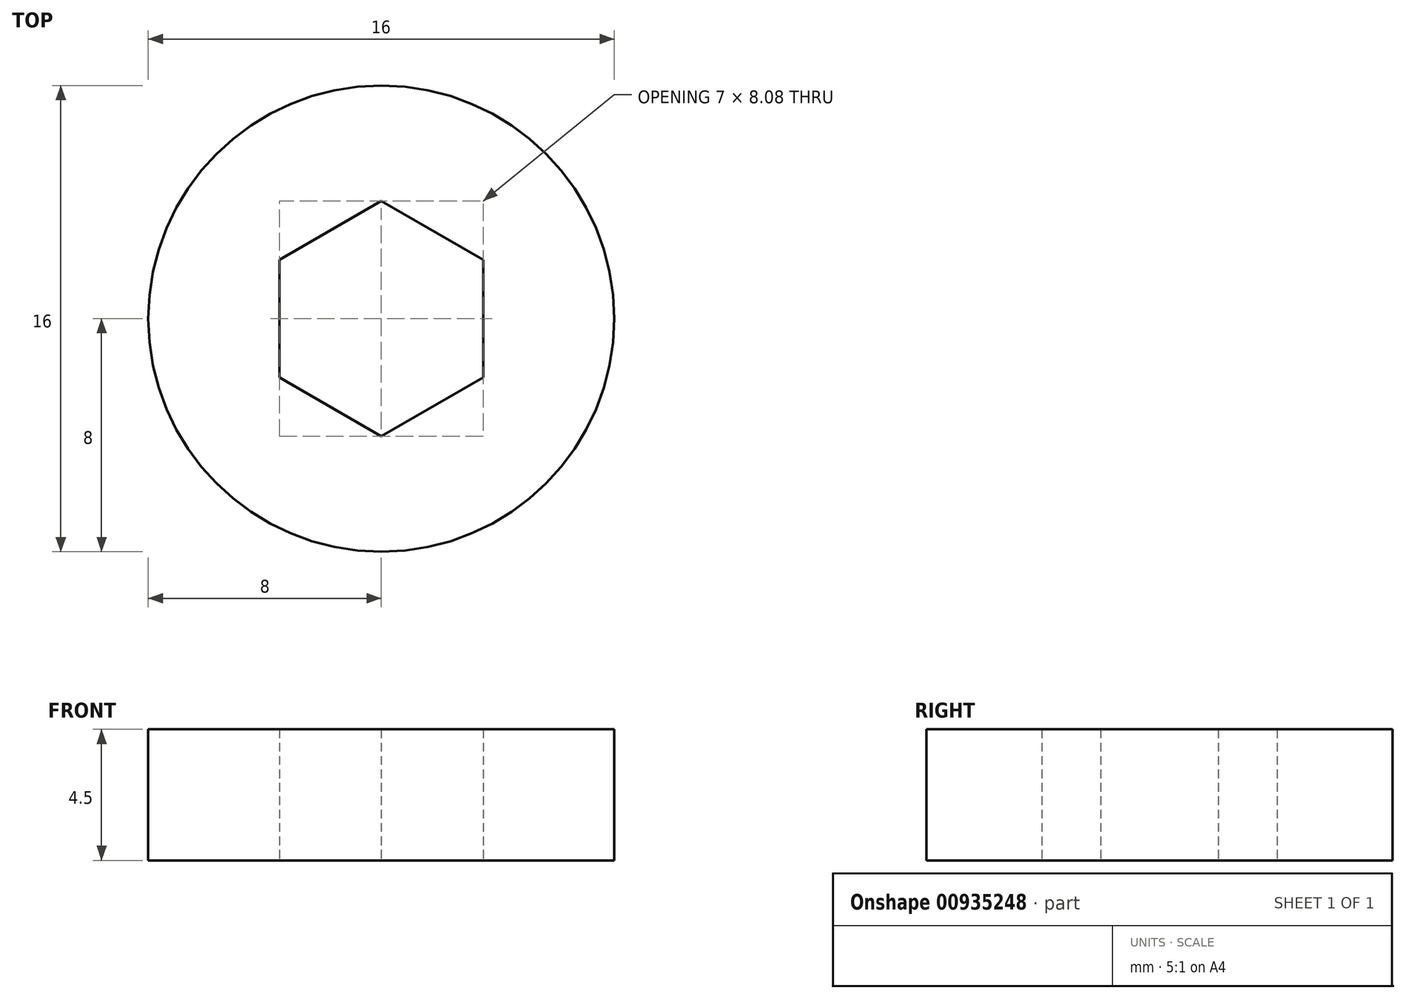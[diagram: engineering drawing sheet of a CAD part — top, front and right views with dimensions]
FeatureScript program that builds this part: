
annotation { "Feature Type Name" : "Feature", "Feature Type Description" : "" }
export const myFeature = defineFeature(function(context is Context, id is Id, definition is map)
    precondition{}
    {
        {
            var Q0;
            Q0=qCreatedBy(makeId("Top.planeOp"),FACE);
            var sketch = newSketch(context, id + "F0", { "sketchPlane" : qUnion([Q0])});
            skCircle(sketch, "E0", {"center": v(0, 0) * mm, "radius": 8 * mm});
            skCircle(sketch, "E1", {"center": v(0, 0) * mm, "radius": 3.5 * mm});
            skCircle(sketch, "E2.cCircle", {"center": v(0, 0) * mm, "radius": 3.5 * mm, "construction": true});
            skLineSegment(sketch, "E2.0", {"start": v(3.5, 2.02) * mm, "end": v(3.5, -2.02) * mm});
            skLineSegment(sketch, "E2.1", {"start": v(3.5, -2.02) * mm, "end": v(0, -4.04) * mm});
            skLineSegment(sketch, "E2.2", {"start": v(0, -4.04) * mm, "end": v(-3.5, -2.02) * mm});
            skLineSegment(sketch, "E2.3", {"start": v(-3.5, -2.02) * mm, "end": v(-3.5, 2.02) * mm});
            skLineSegment(sketch, "E2.4", {"start": v(-3.5, 2.02) * mm, "end": v(0, 4.04) * mm});
            skLineSegment(sketch, "E2.5", {"start": v(0, 4.04) * mm, "end": v(3.5, 2.02) * mm});
            skPoint(sketch, "E2.0.midPoint", {"position": v(3.5, 0) * mm});
            skSolve(sketch);
        }
        {
            var Q0;
            Q0=makeQuery(id+"F0.imprint","IMPRINT",FACE,{"disambiguationData":[TD([[makeQuery(id+"F0.imprint","IMPRINT",EDGE,{"derivedFrom":sQuery(id+"F0.wireOp",EDGE,"E0")}),1.0]])]});
            extrude(context, id + "F1", {"entities" : qUnion([Q0]), "depth" : 4.5 * mm, "offsetDistance" : 25 * mm});
        }
    });
